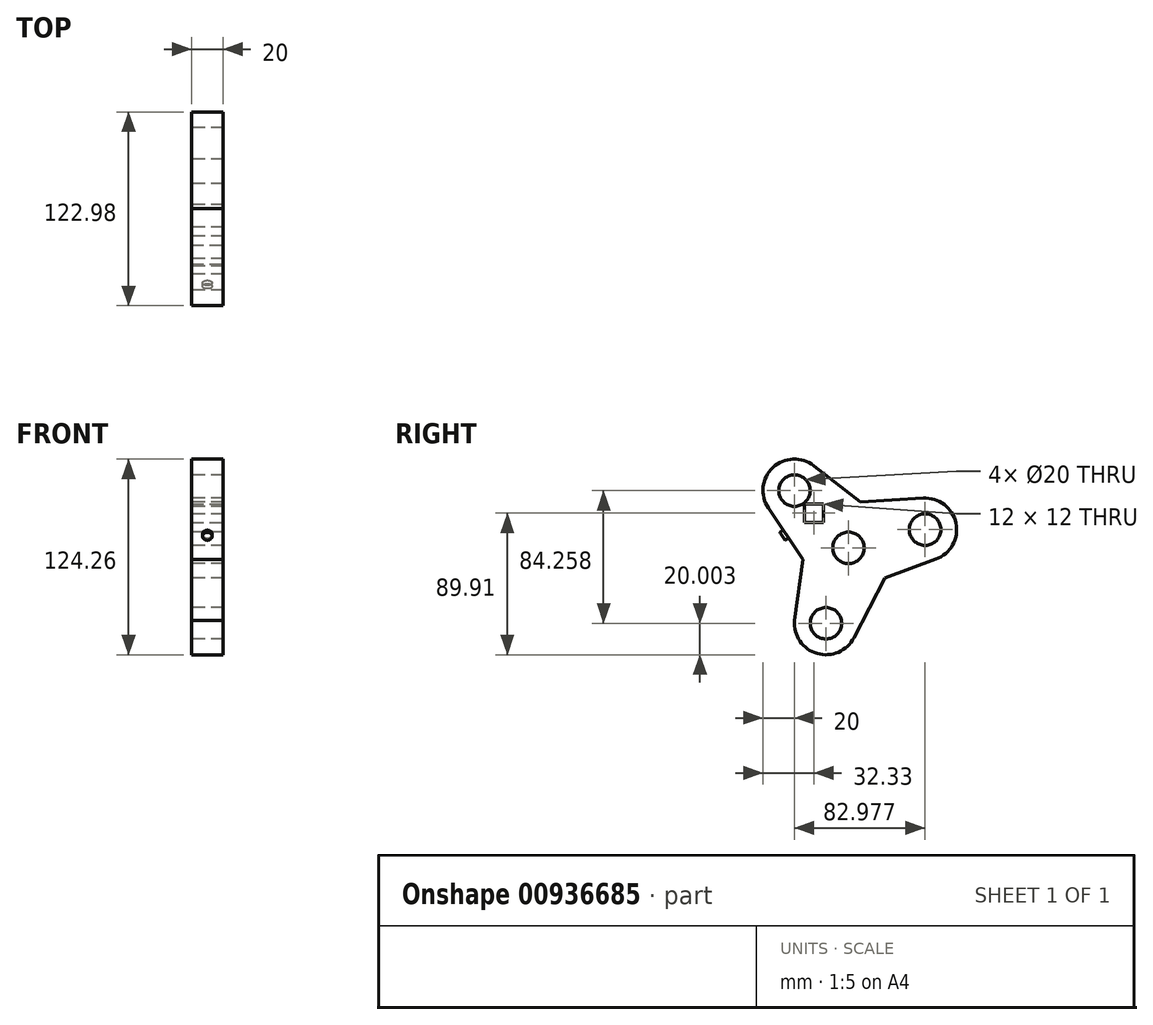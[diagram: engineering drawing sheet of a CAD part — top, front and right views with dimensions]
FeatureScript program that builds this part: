
annotation { "Feature Type Name" : "Feature", "Feature Type Description" : "" }
export const myFeature = defineFeature(function(context is Context, id is Id, definition is map)
    precondition{}
    {
        {
            var Q0;
            Q0=qCreatedBy(makeId("Right.planeOp"),FACE);
            var sketch = newSketch(context, id + "F0", { "sketchPlane" : qUnion([Q0])});
            skCircle(sketch, "E0", {"center": v(-34.33, 36.35) * mm, "radius": 10 * mm});
            skCircle(sketch, "E1", {"center": v(48.65, 11.55) * mm, "radius": 10 * mm});
            skCircle(sketch, "E2", {"center": v(-14.32, -47.9) * mm, "radius": 10 * mm});
            skCircle(sketch, "E3", {"center": v(0, 0) * mm, "radius": 10 * mm});
            skArc(sketch, "E4", {"start": v(-22.01, 52.1) * mm, "mid": v(-47.95, 51) * mm, "end": v(-50.94, 25.2) * mm});
            skArc(sketch, "E5", {"start": v(55.54, -7.22) * mm, "mid": v(68.22, 15.66) * mm, "end": v(47.41, 31.52) * mm});
            skArc(sketch, "E6", {"start": v(-34, -44.33) * mm, "mid": v(-20.77, -66.84) * mm, "end": v(3.44, -57.1) * mm});
            skCircle(sketch, "E7", {"center": v(0, 0) * mm, "radius": 30 * mm});
            skLineSegment(sketch, "E8", {"start": v(3.44, -57.1) * mm, "end": v(23.1, -19.14) * mm});
            skLineSegment(sketch, "E9", {"start": v(23.1, -19.14) * mm, "end": v(55.54, -7.22) * mm});
            skLineSegment(sketch, "E10", {"start": v(-34.24, -46.21) * mm, "end": v(-29.08, -7.37) * mm});
            skLineSegment(sketch, "E11", {"start": v(-29.08, -7.37) * mm, "end": v(-50.94, 25.2) * mm});
            skLineSegment(sketch, "E12", {"start": v(-22.01, 52.1) * mm, "end": v(7.48, 29.05) * mm});
            skLineSegment(sketch, "E13", {"start": v(7.48, 29.05) * mm, "end": v(47.41, 31.52) * mm});
            skSolve(sketch);
        }
        {
            var Q0;
            Q0=makeQuery(id+"F0.imprint","IMPRINT",FACE,{"disambiguationData":[TD([[makeQuery(id+"F0.imprint","IMPRINT",EDGE,{"derivedFrom":sQuery(id+"F0.wireOp",EDGE,"E0")}),-1.0]])]});
            var Q1;
            Q1=makeQuery(id+"F0.imprint","IMPRINT",FACE,{"disambiguationData":[TD([[makeQuery(id+"F0.imprint","IMPRINT",EDGE,{"derivedFrom":sQuery(id+"F0.wireOp",EDGE,"E1")}),-1.0]])]});
            var Q2;
            Q2=makeQuery(id+"F0.imprint","IMPRINT",FACE,{"disambiguationData":[TD([[makeQuery(id+"F0.imprint","IMPRINT",EDGE,{"derivedFrom":sQuery(id+"F0.wireOp",EDGE,"E2")}),-1.0]])]});
            var Q3;
            Q3=makeQuery(id+"F0.imprint","IMPRINT",FACE,{"disambiguationData":[TD([[makeQuery(id+"F0.imprint","IMPRINT",EDGE,{"derivedFrom":sQuery(id+"F0.wireOp",EDGE,"E3")}),-1.0]])]});
            extrude(context, id + "F1", {"entities" : qUnion([Q0, Q1, Q2, Q3]), "depth" : 20 * mm, "offsetDistance" : 25 * mm});
        }
        {
            var Q0;
            Q0=makeQuery(id+"F1.opExtrude","SWEPT_FACE",FACE,{"disambiguationData":[OSD([sQuery(id+"F0.wireOp",EDGE,"E11")])]});
            var sketch = newSketch(context, id + "F2", { "sketchPlane" : qUnion([Q0])});
            skCircle(sketch, "E14", {"center": v(10, 29.46) * mm, "radius": 3 * mm});
            skSolve(sketch);
        }
        {
            var Q0;
            Q0=makeQuery(id+"F2.imprint","IMPRINT",FACE,{"disambiguationData":[TD([[makeQuery(id+"F2.imprint","IMPRINT",EDGE,{"derivedFrom":sQuery(id+"F2.wireOp",EDGE,"E14")}),1.0]])]});
            extrude(context, id + "F3", {"entities" : qUnion([Q0]), "operationType" : NewBodyOperationType.ADD, "endBound" : BoundingType.SYMMETRIC, "depth" : 5 * mm, "offsetDistance" : 25 * mm});
        }
        {
            var Q0;
            Q0=makeQuery(id+"F1.opExtrude","CAP_FACE",FACE,{"disambiguationData":[OSD([sQuery(id+"F0.wireOp",EDGE,"E0"),sQuery(id+"F0.wireOp",EDGE,"E1"),sQuery(id+"F0.wireOp",EDGE,"E2"),sQuery(id+"F0.wireOp",EDGE,"E3"),sQuery(id+"F0.wireOp",EDGE,"E4"),sQuery(id+"F0.wireOp",EDGE,"E5"),sQuery(id+"F0.wireOp",EDGE,"E6"),sQuery(id+"F0.wireOp",EDGE,"E8"),sQuery(id+"F0.wireOp",EDGE,"E9"),sQuery(id+"F0.wireOp",EDGE,"E10"),sQuery(id+"F0.wireOp",EDGE,"E11"),sQuery(id+"F0.wireOp",EDGE,"E12"),sQuery(id+"F0.wireOp",EDGE,"E13")])],"isStart":false});
            var sketch = newSketch(context, id + "F4", { "sketchPlane" : qUnion([Q0])});
            skLineSegment(sketch, "E15.bottom", {"start": v(-28, 28) * mm, "end": v(-16, 28) * mm});
            skLineSegment(sketch, "E15.top", {"start": v(-28, 16) * mm, "end": v(-16, 16) * mm});
            skLineSegment(sketch, "E15.left", {"start": v(-28, 28) * mm, "end": v(-28, 16) * mm});
            skLineSegment(sketch, "E15.right", {"start": v(-16, 28) * mm, "end": v(-16, 16) * mm});
            skSolve(sketch);
        }
        {
            var Q0;
            Q0=makeQuery(id+"F4.imprint","IMPRINT",FACE,{"disambiguationData":[TD([[makeQuery(id+"F4.imprint","IMPRINT",EDGE,{"derivedFrom":sQuery(id+"F4.wireOp",EDGE,"E15.bottom")}),-1.0]])]});
            extrude(context, id + "F5", {"entities" : qUnion([Q0]), "operationType" : NewBodyOperationType.REMOVE, "oppositeDirection" : true, "depth" : 30 * mm, "offsetDistance" : 25 * mm});
        }
    });
